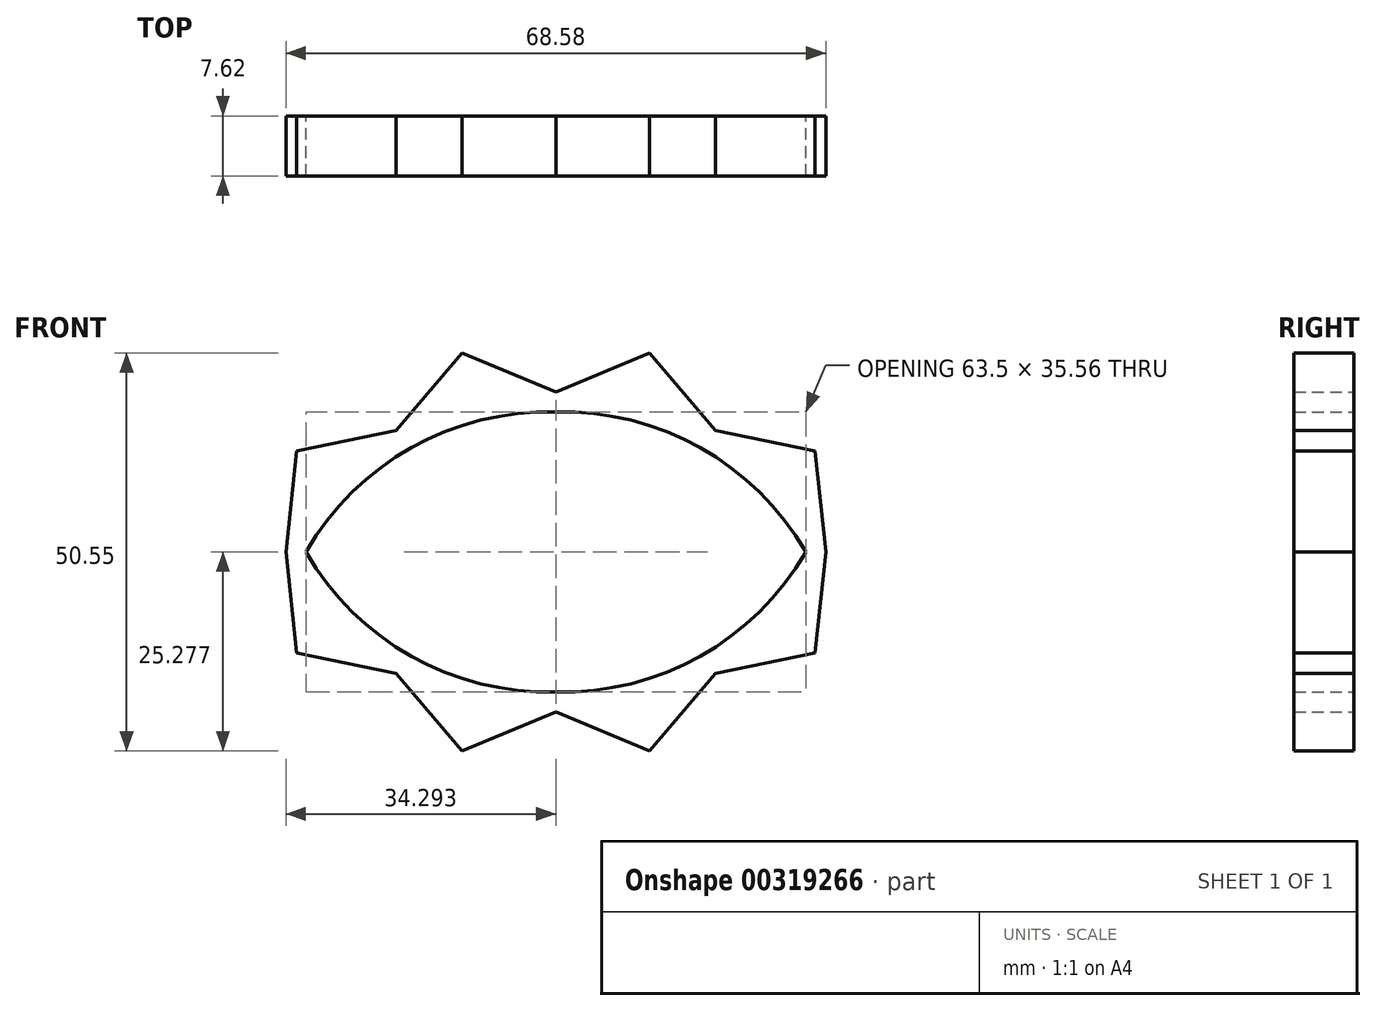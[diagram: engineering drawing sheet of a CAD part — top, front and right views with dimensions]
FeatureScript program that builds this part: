
annotation { "Feature Type Name" : "Feature", "Feature Type Description" : "" }
export const myFeature = defineFeature(function(context is Context, id is Id, definition is map)
    precondition{}
    {
        {
            var Q0;
            Q0=qCreatedBy(makeId("Front.planeOp"),FACE);
            var sketch = newSketch(context, id + "F0", { "sketchPlane" : qUnion([Q0])});
            skLineSegment(sketch, "E0", {"start": v(-13.5, 12.84) * mm, "end": v(50, 12.84) * mm});
            skLineSegment(sketch, "E1", {"start": v(18.25, 12.84) * mm, "end": v(18.25, 30.62) * mm});
            skLineSegment(sketch, "E2", {"start": v(18.25, 12.84) * mm, "end": v(18.25, -4.94) * mm});
            skArc(sketch, "E3", {"start": v(18.25, 30.62) * mm, "mid": v(-0.07, 26.1) * mm, "end": v(-13.5, 12.84) * mm});
            skArc(sketch, "E4", {"start": v(50, 12.84) * mm, "mid": v(36.57, 26.1) * mm, "end": v(18.25, 30.62) * mm});
            skArc(sketch, "E5", {"start": v(18.25, -4.94) * mm, "mid": v(36.57, -0.42) * mm, "end": v(50, 12.84) * mm});
            skArc(sketch, "E6", {"start": v(-13.5, 12.84) * mm, "mid": v(-0.07, -0.42) * mm, "end": v(18.25, -4.94) * mm});
            skLineSegment(sketch, "E7", {"start": v(-13.5, 12.84) * mm, "end": v(-16.04, 12.84) * mm});
            skLineSegment(sketch, "E8", {"start": v(18.25, 30.62) * mm, "end": v(18.25, 33.16) * mm});
            skArc(sketch, "E9", {"start": v(18.25, 33.16) * mm, "mid": v(-2, 28.25) * mm, "end": v(-16.04, 12.84) * mm});
            skLineSegment(sketch, "E10", {"start": v(50, 12.84) * mm, "end": v(52.54, 12.84) * mm});
            skArc(sketch, "E11", {"start": v(52.54, 12.84) * mm, "mid": v(38.51, 28.25) * mm, "end": v(18.25, 33.16) * mm});
            skLineSegment(sketch, "E12", {"start": v(18.25, -4.94) * mm, "end": v(18.25, -7.48) * mm});
            skArc(sketch, "E13", {"start": v(-16.04, 12.84) * mm, "mid": v(-2, -2.58) * mm, "end": v(18.25, -7.48) * mm});
            skArc(sketch, "E14", {"start": v(18.25, -7.48) * mm, "mid": v(38.51, -2.58) * mm, "end": v(52.54, 12.84) * mm});
            skPoint(sketch, "E15", {"position": v(-2, 28.25) * mm});
            skLineSegment(sketch, "E16", {"start": v(-16.04, 12.84) * mm, "end": v(-14.66, 25.67) * mm});
            skLineSegment(sketch, "E17", {"start": v(-14.66, 25.67) * mm, "end": v(-2, 28.25) * mm});
            skLineSegment(sketch, "E18", {"start": v(-2, 28.25) * mm, "end": v(6.33, 38.11) * mm});
            skLineSegment(sketch, "E19", {"start": v(6.33, 38.11) * mm, "end": v(18.25, 33.16) * mm});
            skLineSegment(sketch, "E20", {"start": v(6.33, 38.11) * mm, "end": v(-2, 28.25) * mm});
            skLineSegment(sketch, "E21", {"start": v(18.25, 33.16) * mm, "end": v(-2, 28.25) * mm});
            skLineSegment(sketch, "E22", {"start": v(8.12, 30.7) * mm, "end": v(6.33, 38.11) * mm});
            skLineSegment(sketch, "E23", {"start": v(-16.04, 12.84) * mm, "end": v(-2, 28.25) * mm});
            skLineSegment(sketch, "E24", {"start": v(-9.02, 20.54) * mm, "end": v(-14.66, 25.67) * mm});
            skPoint(sketch, "E25", {"position": v(38.51, 28.25) * mm});
            skLineSegment(sketch, "E26", {"start": v(18.25, 33.16) * mm, "end": v(30.18, 38.11) * mm});
            skLineSegment(sketch, "E27", {"start": v(30.18, 38.11) * mm, "end": v(38.51, 28.25) * mm});
            skLineSegment(sketch, "E28", {"start": v(18.25, 33.16) * mm, "end": v(38.51, 28.25) * mm});
            skLineSegment(sketch, "E29", {"start": v(28.38, 30.7) * mm, "end": v(30.18, 38.11) * mm});
            skLineSegment(sketch, "E30", {"start": v(38.51, 28.25) * mm, "end": v(51.16, 25.67) * mm});
            skLineSegment(sketch, "E31", {"start": v(51.16, 25.67) * mm, "end": v(52.54, 12.84) * mm});
            skLineSegment(sketch, "E32", {"start": v(38.51, 28.25) * mm, "end": v(52.54, 12.84) * mm});
            skLineSegment(sketch, "E33", {"start": v(45.53, 20.54) * mm, "end": v(51.16, 25.67) * mm});
            skPoint(sketch, "E34", {"position": v(38.51, -2.58) * mm});
            skPoint(sketch, "E35", {"position": v(-2, -2.58) * mm});
            skLineSegment(sketch, "E36", {"start": v(-16.04, 12.84) * mm, "end": v(-14.66, 0) * mm});
            skLineSegment(sketch, "E37", {"start": v(-14.66, 0) * mm, "end": v(-2, -2.58) * mm});
            skLineSegment(sketch, "E38", {"start": v(-2, -2.58) * mm, "end": v(6.33, -12.44) * mm});
            skLineSegment(sketch, "E39", {"start": v(6.33, -12.44) * mm, "end": v(18.25, -7.48) * mm});
            skLineSegment(sketch, "E40", {"start": v(18.25, -7.48) * mm, "end": v(30.18, -12.44) * mm});
            skLineSegment(sketch, "E41", {"start": v(30.18, -12.44) * mm, "end": v(38.51, -2.58) * mm});
            skLineSegment(sketch, "E42", {"start": v(38.51, -2.58) * mm, "end": v(51.16, 0) * mm});
            skLineSegment(sketch, "E43", {"start": v(52.54, 12.84) * mm, "end": v(51.16, 0) * mm});
            skLineSegment(sketch, "E44", {"start": v(-16.04, 12.84) * mm, "end": v(-2, -2.58) * mm});
            skLineSegment(sketch, "E45", {"start": v(-9.02, 5.13) * mm, "end": v(-14.66, 0) * mm});
            skLineSegment(sketch, "E46", {"start": v(-2, -2.58) * mm, "end": v(18.25, -7.48) * mm});
            skLineSegment(sketch, "E47", {"start": v(8.12, -5.03) * mm, "end": v(6.33, -12.44) * mm});
            skLineSegment(sketch, "E48", {"start": v(18.25, -7.48) * mm, "end": v(38.51, -2.58) * mm});
            skLineSegment(sketch, "E49", {"start": v(28.38, -5.03) * mm, "end": v(30.18, -12.44) * mm});
            skLineSegment(sketch, "E50", {"start": v(52.54, 12.84) * mm, "end": v(38.51, -2.58) * mm});
            skLineSegment(sketch, "E51", {"start": v(45.53, 5.13) * mm, "end": v(51.16, 0) * mm});
            skSolve(sketch);
        }
        {
            var Q0;
            Q0 = qSketchRegion(id + "F0", true);
            extrude(context, id + "F1", {"entities" : qUnion([Q0]), "depth" : 7.62 * mm});
        }
    });
